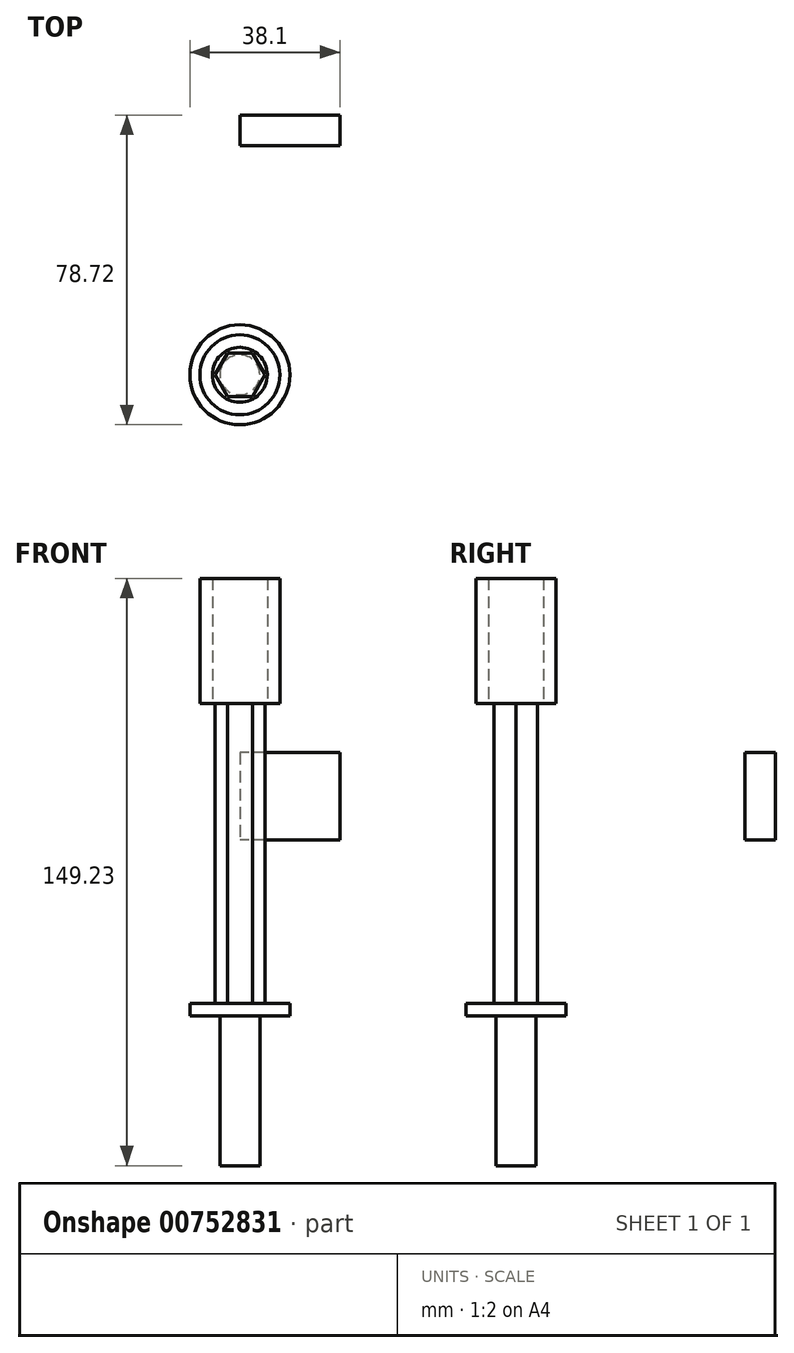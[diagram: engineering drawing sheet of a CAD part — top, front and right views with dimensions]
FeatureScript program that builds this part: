
annotation { "Feature Type Name" : "Feature", "Feature Type Description" : "" }
export const myFeature = defineFeature(function(context is Context, id is Id, definition is map)
    precondition{}
    {
        {
            var Q0;
            Q0=qCreatedBy(makeId("Front.planeOp"),FACE);
            var sketch = newSketch(context, id + "F0", { "sketchPlane" : qUnion([Q0])});
            skLineSegment(sketch, "E0.bottom", {"start": v(0, -39.89) * mm, "end": v(-5.08, -39.89) * mm});
            skLineSegment(sketch, "E0.left", {"start": v(0, -39.89) * mm, "end": v(0, -1.79) * mm});
            skLineSegment(sketch, "E0.right", {"start": v(-5.08, -39.89) * mm, "end": v(-5.08, -1.79) * mm});
            skLineSegment(sketch, "E1.bottom", {"start": v(-12.7, -1.79) * mm, "end": v(-5.08, -1.79) * mm});
            skLineSegment(sketch, "E1.top", {"start": v(-12.7, 1.39) * mm, "end": v(0, 1.39) * mm});
            skLineSegment(sketch, "E1.left", {"start": v(-12.7, -1.79) * mm, "end": v(-12.7, 1.39) * mm});
            skLineSegment(sketch, "E1.right", {"start": v(0, -1.79) * mm, "end": v(0, 1.39) * mm});
            skSolve(sketch);
        }
        {
            var Q0;
            Q0 = qSketchRegion(id + "F0", true);
            var Q1;
            Q1=sQuery(id+"F0.wireOp",EDGE,"E0.left");
            revolve(context, id + "F1", {"surfaceOperationType" : NewSurfaceOperationType.NEW, "entities" : qUnion([Q0]), "axis" : qUnion([Q1]), "revolveType" : RevolveType.FULL});
        }
        {
            var Q0;
            Q0=makeQuery(id+"F1.opRevolve","SWEPT_FACE",FACE,{"disambiguationData":[OSD([sQuery(id+"F0.wireOp",EDGE,"E1.top")])]});
            var sketch = newSketch(context, id + "F2", { "sketchPlane" : qUnion([Q0])});
            skLineSegment(sketch, "E2", {"start": v(-6.35, 0) * mm, "end": v(-3.17, -5.5) * mm});
            skLineSegment(sketch, "E3", {"start": v(-3.17, -5.5) * mm, "end": v(3.18, -5.5) * mm});
            skLineSegment(sketch, "E4", {"start": v(3.18, -5.5) * mm, "end": v(6.35, 0) * mm});
            skLineSegment(sketch, "E5", {"start": v(6.35, 0) * mm, "end": v(3.17, 5.5) * mm});
            skLineSegment(sketch, "E6", {"start": v(3.17, 5.5) * mm, "end": v(-3.18, 5.5) * mm});
            skLineSegment(sketch, "E7", {"start": v(-6.35, 0) * mm, "end": v(-3.18, 5.5) * mm});
            skSolve(sketch);
        }
        {
            var Q0;
            Q0 = qSketchRegion(id + "F2", true);
            extrude(context, id + "F3", {"entities" : qUnion([Q0]), "operationType" : NewBodyOperationType.ADD, "depth" : 76.2 * mm, "offsetDistance" : 25.4 * mm});
        }
        {
            var Q0;
            Q0=makeQuery(id+"F3.opExtrude","CAP_FACE",FACE,{"disambiguationData":[OSD([sQuery(id+"F2.wireOp",EDGE,"E2"),sQuery(id+"F2.wireOp",EDGE,"E3"),sQuery(id+"F2.wireOp",EDGE,"E4"),sQuery(id+"F2.wireOp",EDGE,"E5"),sQuery(id+"F2.wireOp",EDGE,"E6"),sQuery(id+"F2.wireOp",EDGE,"E7")])],"isStart":false});
            var sketch = newSketch(context, id + "F4", { "sketchPlane" : qUnion([Q0])});
            skCircle(sketch, "E8", {"center": v(0, 0) * mm, "radius": 6.99 * mm});
            skCircle(sketch, "E9", {"center": v(0, 0) * mm, "radius": 10.16 * mm});
            skSolve(sketch);
        }
        {
            var Q0;
            Q0 = qSketchRegion(id + "F4", true);
            extrude(context, id + "F5", {"entities" : qUnion([Q0]), "depth" : 31.75 * mm, "offsetDistance" : 25.4 * mm});
        }
        {
            var Q0;
            Q0=qCreatedBy(makeId("Right.planeOp"),FACE);
            var sketch = newSketch(context, id + "F6", { "sketchPlane" : qUnion([Q0])});
            skLineSegment(sketch, "E10.bottom", {"start": v(66.02, 65.04) * mm, "end": v(58.23, 65.04) * mm});
            skLineSegment(sketch, "E10.top", {"start": v(66.02, 42.86) * mm, "end": v(58.23, 42.86) * mm});
            skLineSegment(sketch, "E10.left", {"start": v(66.02, 65.04) * mm, "end": v(66.02, 42.86) * mm});
            skLineSegment(sketch, "E10.right", {"start": v(58.23, 65.04) * mm, "end": v(58.23, 42.86) * mm});
            skSolve(sketch);
        }
        {
            var Q0;
            Q0 = qSketchRegion(id + "F6", true);
            extrude(context, id + "F7", {"entities" : qUnion([Q0]), "depth" : 25.4 * mm, "offsetDistance" : 25.4 * mm});
        }
    });
